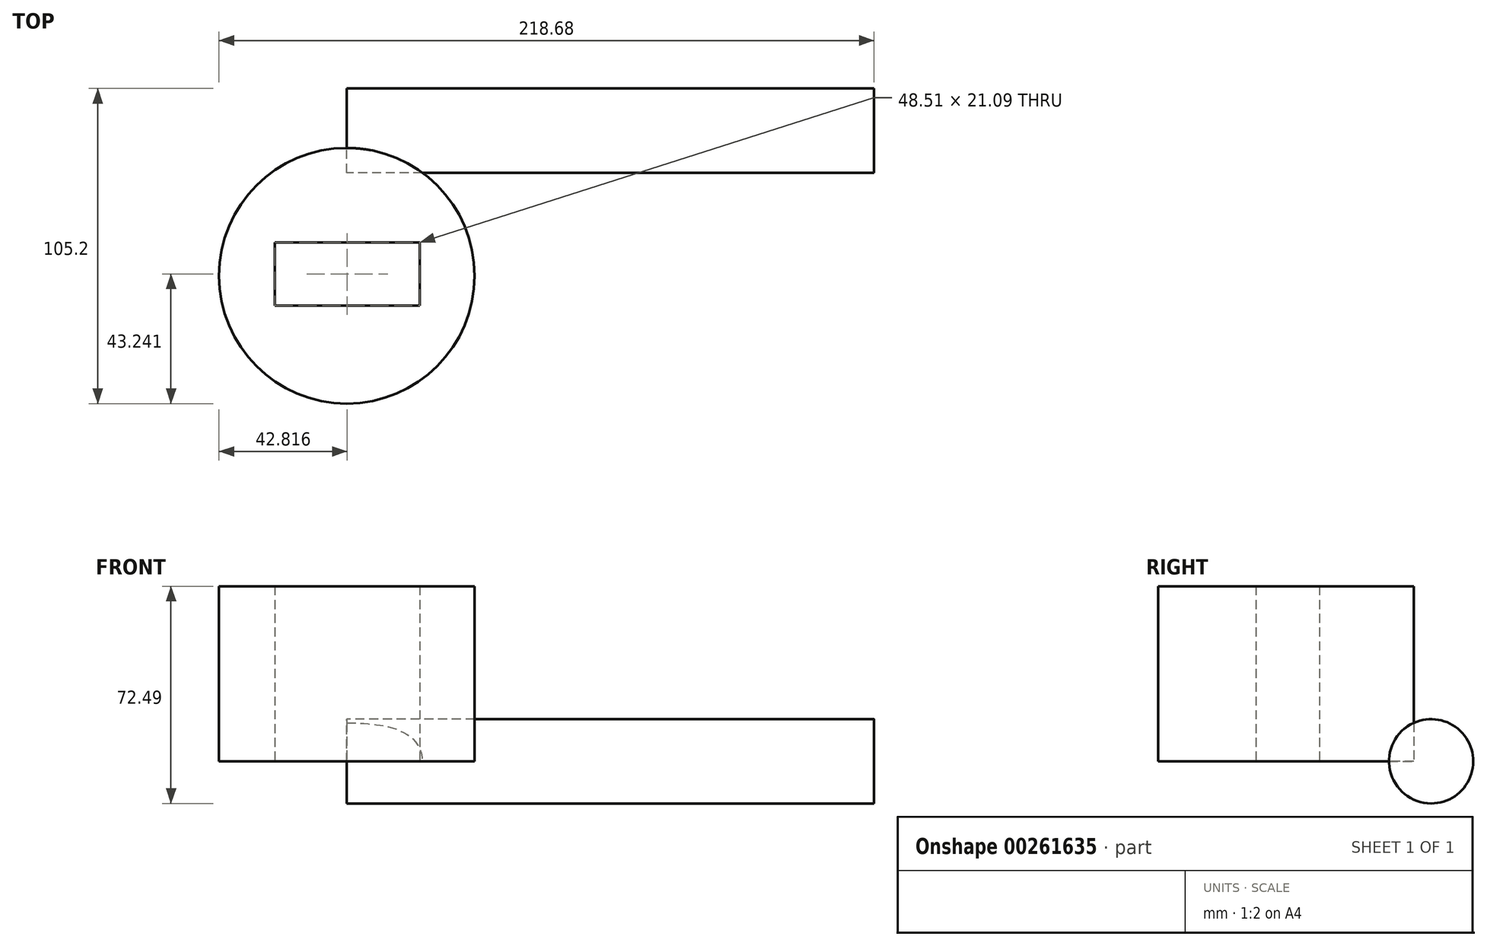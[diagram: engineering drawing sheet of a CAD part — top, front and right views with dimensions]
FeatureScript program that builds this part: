
annotation { "Feature Type Name" : "Feature", "Feature Type Description" : "" }
export const myFeature = defineFeature(function(context is Context, id is Id, definition is map)
    precondition{}
    {
        {
            var Q0;
            Q0=qCreatedBy(makeId("Top.planeOp"),FACE);
            var sketch = newSketch(context, id + "F0", { "sketchPlane" : qUnion([Q0])});
            skCircle(sketch, "E0", {"center": v(0, 0) * mm, "radius": 42.66 * mm});
            skLineSegment(sketch, "E1.bottom", {"start": v(-24.1, 11.13) * mm, "end": v(24.4, 11.13) * mm});
            skLineSegment(sketch, "E1.top", {"start": v(-24.1, -9.96) * mm, "end": v(24.4, -9.96) * mm});
            skLineSegment(sketch, "E1.left", {"start": v(-24.1, 11.13) * mm, "end": v(-24.1, -9.96) * mm});
            skLineSegment(sketch, "E1.right", {"start": v(24.4, 11.13) * mm, "end": v(24.4, -9.96) * mm});
            skSolve(sketch);
        }
        {
            var Q0;
            Q0 = qSketchRegion(id + "F0", true);
            extrude(context, id + "F1", {"entities" : qUnion([Q0]), "depth" : 58.42 * mm});
        }
        {
            var Q0;
            Q0=qCreatedBy(makeId("Right.planeOp"),FACE);
            var sketch = newSketch(context, id + "F2", { "sketchPlane" : qUnion([Q0])});
            skCircle(sketch, "E2", {"center": v(48.47, 0) * mm, "radius": 14.07 * mm});
            skSolve(sketch);
        }
        {
            var Q0;
            Q0=makeQuery(id+"F2.imprint","IMPRINT",FACE,{"disambiguationData":[TD([[makeQuery(id+"F2.imprint","IMPRINT",EDGE,{"derivedFrom":sQuery(id+"F2.wireOp",EDGE,"E2")}),1.0]])]});
            extrude(context, id + "F3", {"entities" : qUnion([Q0]), "operationType" : NewBodyOperationType.ADD, "depth" : 176.02 * mm});
        }
    });
